# Revit family: LAMP_FIL 45 CORNER OPAL COMFORT RECESSED
name_source: partatom
category: Luminarias
revit_build: Autodesk Revit 2018 (Build: 20170223_1515(x64)
units: mm (PartAtom-declared; Revit-internal decimal feet)

## family parameters
Anfitrión = Cara
Compartido = No
Corte con vacíos al cargar = No
Cota de conector redondo = Diámetro de uso
Origen de luz = Sí
Punto de cálculo de habitación = No
Tipo de pieza = Normal

## types (12) — shared parameters
CRI = 80
Cambio de temperatura de color de luz atenuada = <Ninguno>
Dimensions = 318x318
Elevación por defecto = 1219 mm
Fabricante = LAMP
Filtro de color = 16777215
Gear = Electronic
IEE = A+
Installation instructions = https://www.lamp.es
Insulation class = I
LED Lifetime = 70.000 L80 B10
Lamp = MID-POWER LED
Last update = 15/04/2021
MacAdam = 3
Manufacturer URL = http://www.lamp.es
Manufacturer country = Spain
Manufacturer name = LAMP
Material difusor = LAMP_PC Difusor Opal Fil
Material suspension = LAMP_Acero genérico
Plum = 10 W
Power = 8 W
Power Supply = 220-240V 50/60Hz
Product URL = https://www.lamp.es
Product datasheet = http://www.lamp.es
Protection rating = IP20 / IK07
Recessed dimensions = 846x51x0
Type = MID POWER TRIDONIC
Weight = 1.32 kg
Ángulo de inclinación = -90.00°

## per-type parameters (varying)
| type | Archivo de red fotométrica | Descripción | Efficacy | Finish | Indirect light | Material perfil | Modelo | Product code |
| 1300LM 3000K DALI BLACK | F41RECRMOPR830nB.IES | FIL45 CORNER REC 1300 WW OP COMF DALI BK | 87 lm/W | Matte black RAL 9011 | LAMP_FIL 45 CORNER OPAL COMFORT RECESSED_INDIRECT : 1300LM 3000K  BLACK | LAMP_Aluminio Perfil Fil NG | F41RECRMOPR830DB | F41RECRMOPR830DB |
| 1300LM 3000K DALI GREY | F41RECRMOPR830nG.IES | FIL45 CORNER REC 1300 WW OP COMF DALI GR | 87 lm/W | Gloss grey | LAMP_FIL 45 CORNER OPAL COMFORT RECESSED_INDIRECT : 1300LM 3000K  BLACK | LAMP_Aluminio Perfil Fil GR | F41RECRMOPR830DG | F41RECRMOPR830DG |
| 1300LM 3000K DALI WHITE | F41RECRMOPR830nW.IES | FIL45 CORNER REC 1300 WW OP COMF DALI WH | 87 lm/W | Matte white RAL 9010 | LAMP_FIL 45 CORNER OPAL COMFORT RECESSED_INDIRECT : 1300LM 3000K  BLACK | LAMP_Aluminio Perfil Fil BL | F41RECRMOPR830DW | F41RECRMOPR830DW |
| 1300LM 3000K  BLACK | F41RECRMOPR830NB.IES | FIL45 CORNER REC 1300 WW OP COMF BK. | 87 lm/W | Matte black RAL 9011 | LAMP_FIL 45 CORNER OPAL COMFORT RECESSED_INDIRECT : 1300LM 3000K  BLACK | LAMP_Aluminio Perfil Fil NG | F41RECRMOPR830NB | F41RECRMOPR830NB |
| 1300LM 3000K  GREY | F41RECRMOPR830NG.IES | FIL45 CORNER REC 1300 WW OP COMF GR. | 87 lm/W | Gloss grey | LAMP_FIL 45 CORNER OPAL COMFORT RECESSED_INDIRECT : 1300LM 3000K  BLACK | LAMP_Aluminio Perfil Fil GR | F41RECRMOPR830NG | F41RECRMOPR830NG |
| 1300LM 3000K  WHITE | F41RECRMOPR830NW.IES | FIL45 CORNER REC 1300 WW OP COMF WH. | 87 lm/W | Matte white RAL 9010 | LAMP_FIL 45 CORNER OPAL COMFORT RECESSED_INDIRECT : 1300LM 3000K  BLACK | LAMP_Aluminio Perfil Fil BL | F41RECRMOPR830NW | F41RECRMOPR830NW |
| 1300LM 4000K DALI BLACK | F41RECRMOPR840nB.IES | FIL45 CORNER REC 1300 NW OP COMF DALI BK | 91 lm/W | Matte black RAL 9011 | LAMP_FIL 45 CORNER OPAL COMFORT RECESSED_INDIRECT : 1300LM 4000K  BLACK | LAMP_Aluminio Perfil Fil NG | F41RECRMOPR840DB | F41RECRMOPR840DB |
| 1300LM 4000K DALI GREY | F41RECRMOPR840nG.IES | FIL45 CORNER REC 1300 NW OP COMF DALI GR | 91 lm/W | Gloss grey | LAMP_FIL 45 CORNER OPAL COMFORT RECESSED_INDIRECT : 1300LM 4000K  BLACK | LAMP_Aluminio Perfil Fil GR | F41RECRMOPR840DG | F41RECRMOPR840DG |
| 1300LM 4000K DALI WHITE | F41RECRMOPR840nW.IES | FIL45 CORNER REC 1300 NW OP COMF DALI WH | 91 lm/W | Matte white RAL 9010 | LAMP_FIL 45 CORNER OPAL COMFORT RECESSED_INDIRECT : 1300LM 4000K  BLACK | LAMP_Aluminio Perfil Fil BL | F41RECRMOPR840DW | F41RECRMOPR840DW |
| 1300LM 4000K  BLACK | F41RECRMOPR840NB.IES | FIL45 CORNER REC 1300 NW OP COMF BK. | 91 lm/W | Matte black RAL 9011 | LAMP_FIL 45 CORNER OPAL COMFORT RECESSED_INDIRECT : 1300LM 4000K  BLACK | LAMP_Aluminio Perfil Fil NG | F41RECRMOPR840NB | F41RECRMOPR840NB |
| 1300LM 4000K  GREY | F41RECRMOPR840NG.IES | FIL45 CORNER REC 1300 NW OP COMF GR. | 91 lm/W | Gloss grey | LAMP_FIL 45 CORNER OPAL COMFORT RECESSED_INDIRECT : 1300LM 4000K  BLACK | LAMP_Aluminio Perfil Fil GR | F41RECRMOPR840NG | F41RECRMOPR840NG |
| 1300LM 4000K  WHITE | F41RECRMOPR840NW.IES | FIL45 CORNER REC 1300 NW OP COMF WH. | 91 lm/W | Matte white RAL 9010 | LAMP_FIL 45 CORNER OPAL COMFORT RECESSED_INDIRECT : 1300LM 4000K  BLACK | LAMP_Aluminio Perfil Fil BL | F41RECRMOPR840NW | F41RECRMOPR840NW |
